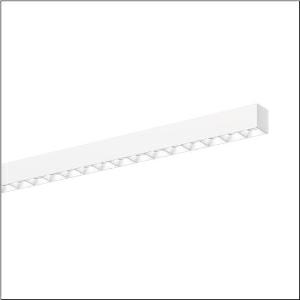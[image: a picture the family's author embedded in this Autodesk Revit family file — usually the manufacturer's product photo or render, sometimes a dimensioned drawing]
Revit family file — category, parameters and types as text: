
# Revit family: silica_r__21_51mx26da44wb_24d1
name_source: partatom
category: Lighting Fixtures
units: mm (PartAtom-declared; Revit-internal decimal feet)

## family parameters
Cut with Voids When Loaded = No
Host = Face
Light Source = No
Part Type = Normal
Room Calculation Point = No
Round Connector Dimension = Use Diameter
Shared = No

## types (1)
- --- (1 x LED, 4320 lm, 23.4 W, 4000K)
    Apparent Load = 23 VA
    CIE Flux Codes = 83 98 100 100 100
    Color Rendering = 80
    Color Temperature = 4000K
    Default Elevation = 1800 mm
    Description = Silica® 21, office luminaire, primary light control with darklight reflector, of PMMA, white, CAT 2 (L<= 3000cd/m²), light emission: direct distribution, primary light characteristic: symmetric, installation type: surface-mounted, LED, rated luminous flux: 4.320lm, luminous efficacy: 185lm/W, light colour: 840, colour temperature: 4000K, with terminal, 3+2-pole, max. 2.5mm², mains connection: 220..240V, AC, 50/60Hz, rated input power: 23.4W, luminaire housing, of aluminium, traffic white (RAL 9016), length: 1.204mm, width: 53mm, height: 53mm, protection rating (complete): IP20, insulation class (complete): insulation class I (protective earthing), certification: CE, permissible operating ambient temperature: 0..+35°C, standard: EN 50419, packaging unit: 1 piece
    Height = 0 mm  [stored 0 ft]
    Lamp = 1 x LED
    Lamp Light Flux = 4320 lm
    Lamp Power = 23.4 W
    Lamp count = 1
    Length = 1204 mm
    Luminous efficacy = 185 lm/W
    Manufacturer = Siteco
    ModVariant = No
    Model = 51MX26DA44WB
    Mounting Place = Ceiling
    Mounting Type = Recessed
    Number of Poles = 1
    OnlyDefault = Yes
    Power Factor = 1
    Product Name = Silica® 21
    Product group = office luminaire | ceiling recessed
    ProductGroupID = 401
    Protection Class = Protection class I
    Protection Degree = IP 20
    RLX_Detail_Level = 1
    RLX_Emergency_Light_Flux = 0 lm
    RLX_Emergency_Type = 0
    RLX_Emergency_Type_DB = No
    RlxData = <blob elided: 38849 chars, md5=7be0a138>
    Socket = socket
    Standby Power = 0 W
    System Light Flux = 4320 lm
    System Power = 23 W
    Type Comments = factory setting: luminous flux: 100 % | dim-lin: 254 | 337 mA
    Type Image = l_1297772.jpg
    URL = http://relux.com
    VarID = @adj_055493
    Voltage = 0 V
    Weight = 0.00 kg
    Width = 53 mm

note: [stored X ft] marks values corroborated as IEEE doubles in the binary element streams (Revit-internal decimal feet)

## geometry (parser evidence)
native form markers: Blend x4, Sweep x10
no freeform markers — native parametric forms only
